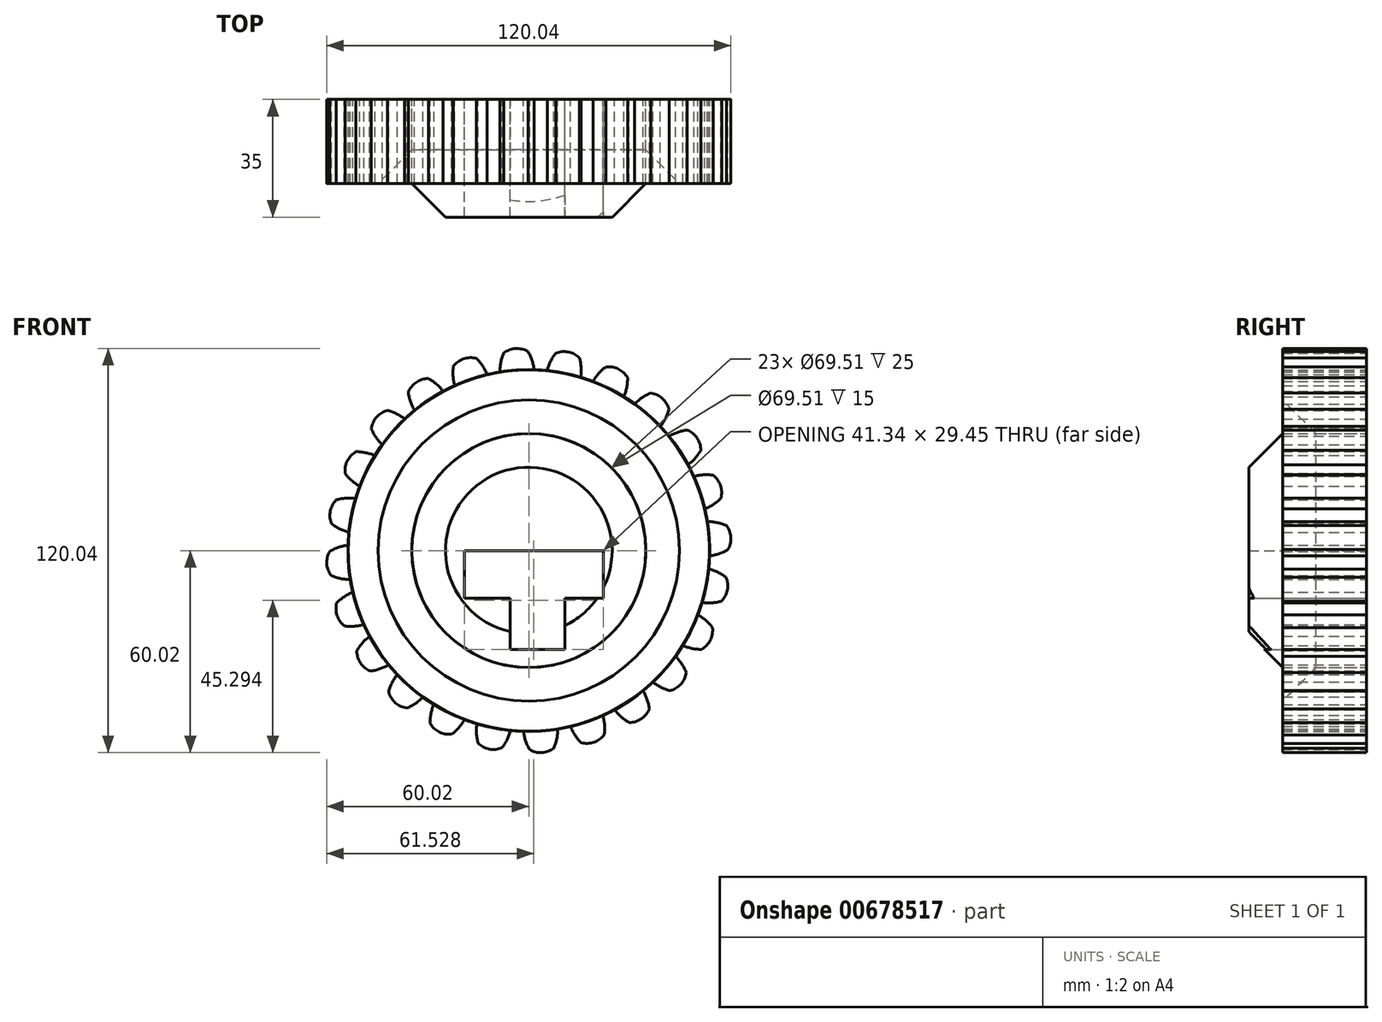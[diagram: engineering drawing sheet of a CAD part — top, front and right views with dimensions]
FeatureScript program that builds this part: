
annotation { "Feature Type Name" : "Feature", "Feature Type Description" : "" }
export const myFeature = defineFeature(function(context is Context, id is Id, definition is map)
    precondition{}
    {
        {
            var Q0;
            Q0=qCreatedBy(makeId("Front.planeOp"),FACE);
            var sketch = newSketch(context, id + "F0", { "sketchPlane" : qUnion([Q0])});
            skCircle(sketch, "E0", {"center": v(0, 0) * mm, "radius": 53.72 * mm});
            skCircle(sketch, "E1", {"center": v(0, 0) * mm, "radius": 58.67 * mm, "construction": true});
            skCircle(sketch, "E2", {"center": v(0, 0) * mm, "radius": 63.5 * mm, "construction": true});
            skLineSegment(sketch, "E3", {"start": v(0, 0) * mm, "end": v(0, 98.32) * mm, "construction": true});
            skLineSegment(sketch, "E4", {"start": v(0, 0) * mm, "end": v(-6.22, 94.86) * mm, "construction": true});
            skLineSegment(sketch, "E5", {"start": v(0, 58.67) * mm, "end": v(-55.1, 51.2) * mm, "construction": true});
            skLineSegment(sketch, "E6", {"start": v(0, 58.67) * mm, "end": v(-57.98, 28.2) * mm, "construction": true});
            skCircle(sketch, "E7", {"center": v(0, 0) * mm, "radius": 51.93 * mm, "construction": true});
            skCircle(sketch, "E8", {"center": v(0, 58.67) * mm, "radius": 14.6 * mm, "construction": true});
            skCircle(sketch, "E9", {"center": v(-12.93, 51.88) * mm, "radius": 14.6 * mm, "construction": true});
            skPoint(sketch, "E10.startSnap0", {"position": v(0, 49.16) * mm});
            skArc(sketch, "E11", {"start": v(-0.27, 59.16) * mm, "mid": v(-1.77, 61.3) * mm, "end": v(-3.63, 63.14) * mm});
            skArc(sketch, "E12", {"start": v(1.56, 53.7) * mm, "mid": v(0.95, 56.53) * mm, "end": v(-0.27, 59.16) * mm});
            skArc(sketch, "E13.MirrorCS", {"start": v(-8.56, 53.03) * mm, "mid": v(-8.32, 55.92) * mm, "end": v(-7.46, 58.69) * mm});
            skArc(sketch, "E14", {"start": v(-0.27, 59.16) * mm, "mid": v(-3.93, 60) * mm, "end": v(-7.46, 58.69) * mm});
            skCircle(sketch, "E15", {"center": v(0, 0) * mm, "radius": 34.75 * mm});
            skLineSegment(sketch, "E16", {"start": v(-19.16, 0) * mm, "end": v(22.18, 0) * mm});
            skLineSegment(sketch, "E17", {"start": v(-19.16, 0) * mm, "end": v(-19.16, -14.13) * mm});
            skLineSegment(sketch, "E18", {"start": v(22.18, 0) * mm, "end": v(22.18, -14.13) * mm});
            skLineSegment(sketch, "E19", {"start": v(22.18, -14.13) * mm, "end": v(10.78, -14.13) * mm});
            skLineSegment(sketch, "E20", {"start": v(-19.16, -14.13) * mm, "end": v(-5.57, -14.13) * mm});
            skLineSegment(sketch, "E21", {"start": v(-5.57, -14.13) * mm, "end": v(-5.57, -29.45) * mm});
            skLineSegment(sketch, "E22", {"start": v(10.78, -14.13) * mm, "end": v(10.78, -29.45) * mm});
            skLineSegment(sketch, "E23", {"start": v(-5.57, -29.45) * mm, "end": v(10.78, -29.45) * mm});
            skSolve(sketch);
        }
        {
            var Q0;
            {var subQ0=sQuery(id+"F0.wireOp",EDGE,"E12");Q0=makeQuery(id+"F0.imprint","IMPRINT",FACE,{"disambiguationData":[TD([[makeQuery(id+"F0.imprint","IMPRINT",EDGE,{"derivedFrom":subQ0}),1.0]])]});}
            var Q1;
            {var subQ0=sQuery(id+"F0.wireOp",EDGE,"E0");var subQ1=makeQuery(id+"F0.imprint","INTERSECT",VERTEX,{"derivedFrom":[subQ0,sQuery(id+"F0.wireOp",EDGE,"E12")]});Q1=makeQuery(id+"F0.imprint","IMPRINT",FACE,{"disambiguationData":[TD([[makeQuery(id+"F0.imprint","IMPRINT",EDGE,{"disambiguationData":[TD([[subQ1,-1.0]])],"derivedFrom":subQ0}),1.0]])]});}
            extrude(context, id + "F1", {"entities" : qUnion([Q0, Q1]), "depth" : 25 * mm, "offsetDistance" : 25 * mm});
        }
        {
            var Q0;
            Q0=makeQuery(id+"F1.opExtrude","SWEPT_BODY",BODY,{"disambiguationData":[OSD([sQuery(id+"F0.wireOp",EDGE,"E0"),sQuery(id+"F0.wireOp",EDGE,"E12"),sQuery(id+"F0.wireOp",EDGE,"E13.MirrorCS"),sQuery(id+"F0.wireOp",EDGE,"E14")])]});
            var Q1;
            Q1=makeQuery(id+"F1.opExtrude","SWEPT_FACE",FACE,{"disambiguationData":[OSD([sQuery(id+"F0.wireOp",EDGE,"E0")])]});
            circularPattern(context, id + "F2", {"entities" : qUnion([Q0]), "axis" : qUnion([Q1]), "angle" : 360 * degree, "instanceCount" : 24, "equalSpace" : true});
        }
        {
            var Q0;
            Q0 = qSketchRegion(id + "F0", true);
            var Q1;
            Q1=makeQuery(id+"F0.imprint","IMPRINT",FACE,{"disambiguationData":[TD([[makeQuery(id+"F0.imprint","IMPRINT",EDGE,{"derivedFrom":sQuery(id+"F0.wireOp",EDGE,"E15")}),1.0]])]});
            extrude(context, id + "F3", {"entities" : qUnion([Q0, Q1]), "depth" : 25 * mm, "offsetDistance" : 25 * mm});
        }
        {
            var Q0;
            Q0=makeQuery(id+"F0.imprint","IMPRINT",FACE,{"disambiguationData":[TD([[makeQuery(id+"F0.imprint","IMPRINT",EDGE,{"derivedFrom":sQuery(id+"F0.wireOp",EDGE,"E15")}),1.0]])]});
            extrude(context, id + "F4", {"entities" : qUnion([Q0]), "depth" : 35 * mm, "offsetDistance" : 25 * mm});
        }
        {
            var Q0;
            Q0=makeQuery(id+"F1.opExtrude","CAP_EDGE",EDGE,{"disambiguationData":[OSD([sQuery(id+"F0.wireOp",EDGE,"E15")])],"isStart":false});
            var Q1;
            Q1=makeQuery(id+"F4.opExtrude","CAP_EDGE",EDGE,{"disambiguationData":[OSD([sQuery(id+"F0.wireOp",EDGE,"E15")])],"isStart":false});
            chamfer(context, id + "F5", {"entities" : qUnion([Q0, Q1]), "width" : 10 * mm, "tangentPropagation" : true});
        }
    });
